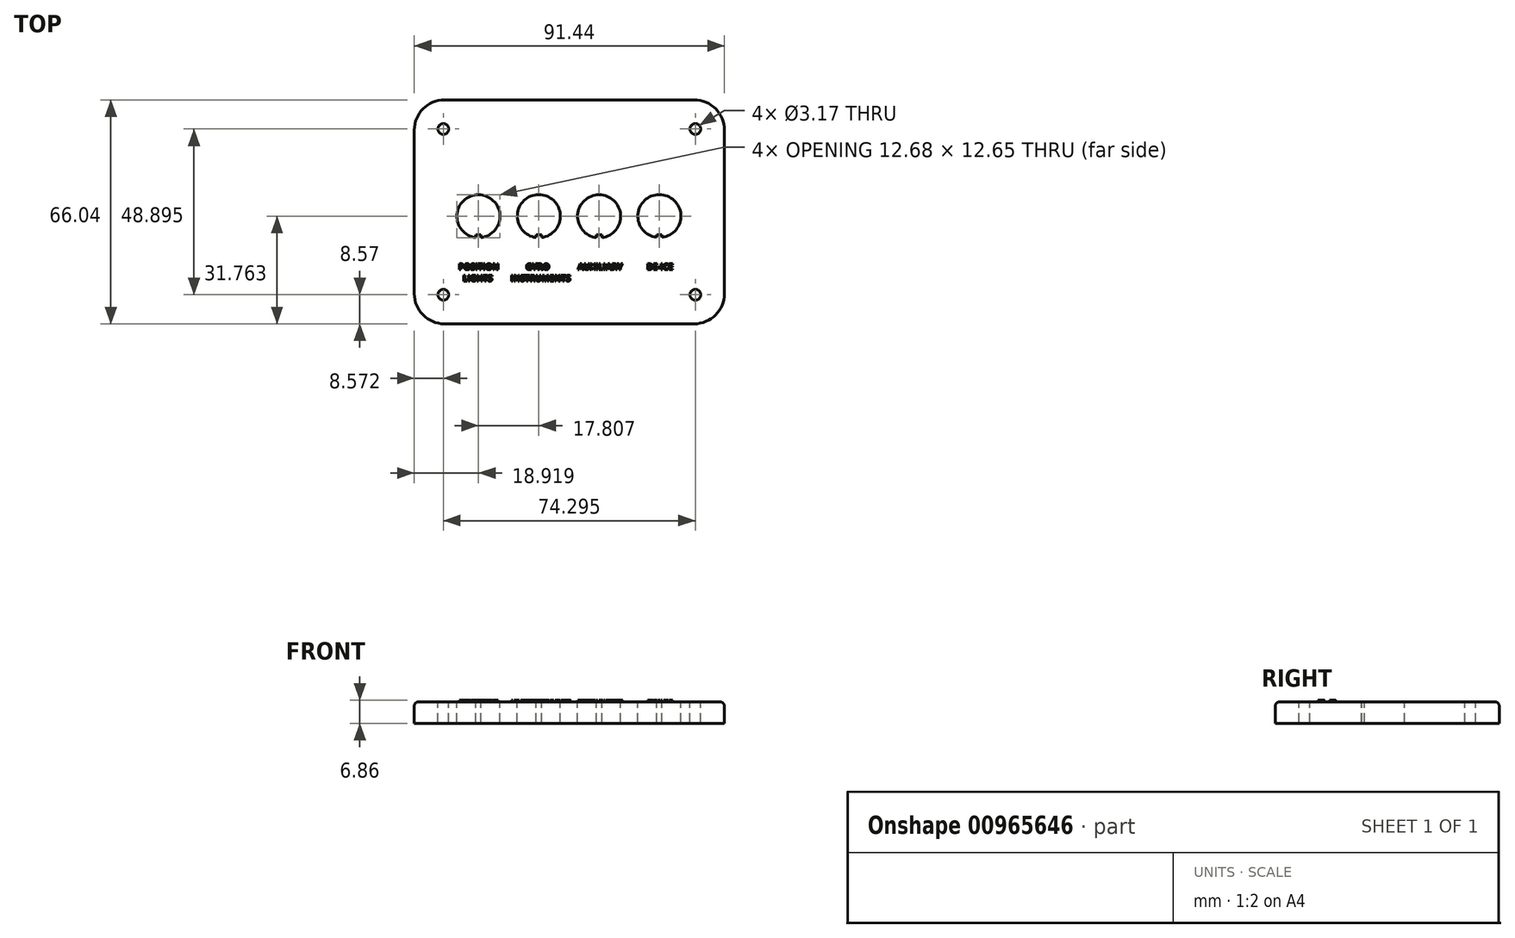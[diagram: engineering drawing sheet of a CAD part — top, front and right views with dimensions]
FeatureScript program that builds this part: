
annotation { "Feature Type Name" : "Feature", "Feature Type Description" : "" }
export const myFeature = defineFeature(function(context is Context, id is Id, definition is map)
    precondition{}
    {
        {
            var Q0;
            Q0=qCreatedBy(makeId("Top.planeOp"),FACE);
            var sketch = newSketch(context, id + "F0", { "sketchPlane" : qUnion([Q0])});
            skPoint(sketch, "E0.middle", {"position": v(-0.12, 0.03) * mm});
            skPoint(sketch, "E1.visualSharp", {"position": v(-44.57, 25.43) * mm});
            skArc(sketch, "E1.filletArc", {"start": v(-37.15, 28.28) * mm, "mid": v(-38.94, 27.54) * mm, "end": v(-39.69, 25.74) * mm});
            skPoint(sketch, "E2.visualSharp", {"position": v(44.33, 25.43) * mm});
            skArc(sketch, "E2.filletArc", {"start": v(39.69, 25.74) * mm, "mid": v(38.94, 27.54) * mm, "end": v(37.15, 28.28) * mm});
            skPoint(sketch, "E3.visualSharp", {"position": v(44.33, -25.37) * mm});
            skArc(sketch, "E3.filletArc", {"start": v(37.15, -25.7) * mm, "mid": v(38.94, -24.95) * mm, "end": v(39.69, -23.15) * mm});
            skPoint(sketch, "E4.visualSharp", {"position": v(-44.57, -25.37) * mm});
            skArc(sketch, "E4.filletArc", {"start": v(-39.69, -23.15) * mm, "mid": v(-38.94, -24.95) * mm, "end": v(-37.15, -25.7) * mm});
            skCircle(sketch, "E5", {"center": v(-37.15, 25.74) * mm, "radius": 1.59 * mm});
            skCircle(sketch, "E6", {"center": v(-37.15, -23.15) * mm, "radius": 1.59 * mm});
            skCircle(sketch, "E7", {"center": v(37.15, -23.15) * mm, "radius": 1.59 * mm});
            skCircle(sketch, "E8", {"center": v(37.15, 25.74) * mm, "radius": 1.59 * mm});
            skLineSegment(sketch, "E9.1", {"start": v(-33.65, -28.55) * mm, "end": v(33.66, -28.55) * mm});
            skLineSegment(sketch, "E9.2", {"start": v(-42.55, -19.66) * mm, "end": v(-42.55, 22.25) * mm});
            skLineSegment(sketch, "E9.5", {"start": v(-33.66, 31.14) * mm, "end": v(33.66, 31.14) * mm});
            skLineSegment(sketch, "E9.7", {"start": v(42.55, -19.66) * mm, "end": v(42.55, 22.25) * mm});
            skLineSegment(sketch, "E10.1", {"start": v(-36.83, -31.72) * mm, "end": v(36.83, -31.72) * mm});
            skLineSegment(sketch, "E10.2", {"start": v(-45.72, -22.83) * mm, "end": v(-45.72, 25.43) * mm});
            skLineSegment(sketch, "E10.5", {"start": v(-36.83, 34.32) * mm, "end": v(36.83, 34.32) * mm});
            skLineSegment(sketch, "E10.7", {"start": v(45.72, -22.83) * mm, "end": v(45.72, 25.43) * mm});
            skPoint(sketch, "E11", {"position": v(-26.79, 0) * mm});
            skPoint(sketch, "E12", {"position": v(-9, 0) * mm});
            skPoint(sketch, "E13", {"position": v(8.77, 0) * mm});
            skPoint(sketch, "E14", {"position": v(26.55, 0) * mm});
            skLineSegment(sketch, "E15.top", {"start": v(27.33, -5.38) * mm, "end": v(25.74, -5.38) * mm});
            skLineSegment(sketch, "E16", {"start": v(25.74, -6.25) * mm, "end": v(25.74, -5.38) * mm});
            skLineSegment(sketch, "E17", {"start": v(27.33, -6.25) * mm, "end": v(27.33, -5.38) * mm});
            skArc(sketch, "E18", {"start": v(27.33, -6.25) * mm, "mid": v(26.54, 6.4) * mm, "end": v(25.74, -6.25) * mm});
            skLineSegment(sketch, "E19.top", {"start": v(9.58, -5.43) * mm, "end": v(7.99, -5.43) * mm});
            skLineSegment(sketch, "E20", {"start": v(7.99, -6.3) * mm, "end": v(7.99, -5.43) * mm});
            skLineSegment(sketch, "E21", {"start": v(9.58, -6.3) * mm, "end": v(9.58, -5.43) * mm});
            skArc(sketch, "E22", {"start": v(9.58, -6.3) * mm, "mid": v(8.78, 6.35) * mm, "end": v(7.99, -6.3) * mm});
            skLineSegment(sketch, "E23.top", {"start": v(-8.2, -5.4) * mm, "end": v(-9.79, -5.4) * mm});
            skLineSegment(sketch, "E24", {"start": v(-9.79, -6.26) * mm, "end": v(-9.79, -5.4) * mm});
            skLineSegment(sketch, "E25", {"start": v(-8.2, -6.26) * mm, "end": v(-8.2, -5.4) * mm});
            skArc(sketch, "E26", {"start": v(-8.2, -6.26) * mm, "mid": v(-9, 6.4) * mm, "end": v(-9.79, -6.26) * mm});
            skLineSegment(sketch, "E27.top", {"start": v(-26, -5.42) * mm, "end": v(-27.6, -5.42) * mm});
            skLineSegment(sketch, "E28", {"start": v(-27.6, -6.28) * mm, "end": v(-27.6, -5.42) * mm});
            skLineSegment(sketch, "E29", {"start": v(-26, -6.28) * mm, "end": v(-26, -5.42) * mm});
            skArc(sketch, "E30", {"start": v(-26, -6.28) * mm, "mid": v(-26.8, 6.37) * mm, "end": v(-27.6, -6.28) * mm});
            skText(sketch, "E31", { "text": "POSITION\n  LIGHTS", "fontName": "OpenSans-Bold.ttf"});
            skText(sketch, "E32", { "text": "       GYRO\nINSTRUMENTS", "fontName": "OpenSans-Bold.ttf"});
            skText(sketch, "E33", { "text": "DE-ICE", "fontName": "OpenSans-Bold.ttf"});
            skText(sketch, "E34", { "text": "AUXILIARY", "fontName": "OpenSans-Bold.ttf"});
            skPoint(sketch, "E35.visualSharp", {"position": v(-45.72, 34.32) * mm});
            skArc(sketch, "E35.filletArc", {"start": v(-36.83, 34.32) * mm, "mid": v(-43.12, 31.71) * mm, "end": v(-45.72, 25.43) * mm});
            skPoint(sketch, "E36.visualSharp", {"position": v(45.72, 34.32) * mm});
            skArc(sketch, "E36.filletArc", {"start": v(45.72, 25.43) * mm, "mid": v(43.12, 31.71) * mm, "end": v(36.83, 34.32) * mm});
            skPoint(sketch, "E37.visualSharp", {"position": v(45.72, -31.72) * mm});
            skArc(sketch, "E37.filletArc", {"start": v(36.83, -31.72) * mm, "mid": v(43.12, -29.12) * mm, "end": v(45.72, -22.83) * mm});
            skPoint(sketch, "E38.visualSharp", {"position": v(-45.72, -31.72) * mm});
            skArc(sketch, "E38.filletArc", {"start": v(-45.72, -22.83) * mm, "mid": v(-43.12, -29.12) * mm, "end": v(-36.83, -31.72) * mm});
            skPoint(sketch, "E39.visualSharp", {"position": v(-42.55, -28.55) * mm});
            skArc(sketch, "E39.filletArc", {"start": v(-42.55, -19.66) * mm, "mid": v(-39.94, -25.94) * mm, "end": v(-33.65, -28.55) * mm});
            skPoint(sketch, "E40.visualSharp", {"position": v(-42.55, 31.14) * mm});
            skArc(sketch, "E40.filletArc", {"start": v(-33.66, 31.14) * mm, "mid": v(-39.94, 28.54) * mm, "end": v(-42.55, 22.25) * mm});
            skPoint(sketch, "E41.visualSharp", {"position": v(42.55, 31.14) * mm});
            skArc(sketch, "E41.filletArc", {"start": v(42.55, 22.25) * mm, "mid": v(39.94, 28.54) * mm, "end": v(33.66, 31.14) * mm});
            skPoint(sketch, "E42.visualSharp", {"position": v(42.55, -28.55) * mm});
            skArc(sketch, "E42.filletArc", {"start": v(33.66, -28.55) * mm, "mid": v(39.94, -25.94) * mm, "end": v(42.55, -19.66) * mm});
            const initialGuessF0  = {"E31": [-0.03267, -0.01575, 1, 0, 0.00178], "E32": [-0.0173, -0.01575, 1, 0, 0.00178], "E33": [0.02284, -0.01575, 1, 0, 0.00178], "E34": [0.00253, -0.01575, 1, 0, 0.00178]};
            skSetInitialGuess(sketch, initialGuessF0);
            skSolve(sketch);
        }
        {
            var Q0;
            Q0=makeQuery(id+"F0.imprint","IMPRINT",FACE,{"disambiguationData":[TD([[makeQuery(id+"F0.imprint","IMPRINT",EDGE,{"derivedFrom":sQuery(id+"F0.wireOp",EDGE,"E31.sketch_text.stroke-0")}),1.0]])]});
            var Q1;
            Q1=makeQuery(id+"F0.imprint","IMPRINT",FACE,{"disambiguationData":[TD([[makeQuery(id+"F0.imprint","IMPRINT",EDGE,{"derivedFrom":sQuery(id+"F0.wireOp",EDGE,"E31.sketch_text.stroke-24")}),1.0]])]});
            var Q2;
            Q2=makeQuery(id+"F0.imprint","IMPRINT",FACE,{"disambiguationData":[TD([[makeQuery(id+"F0.imprint","IMPRINT",EDGE,{"derivedFrom":sQuery(id+"F0.wireOp",EDGE,"E31.sketch_text.stroke-82")}),1.0]])]});
            var Q3;
            Q3=makeQuery(id+"F0.imprint","IMPRINT",FACE,{"disambiguationData":[TD([[makeQuery(id+"F0.imprint","IMPRINT",EDGE,{"derivedFrom":sQuery(id+"F0.wireOp",EDGE,"E33.sketch_text.stroke-7")}),1.0]])]});
            var Q4;
            Q4=makeQuery(id+"F0.imprint","IMPRINT",FACE,{"disambiguationData":[TD([[makeQuery(id+"F0.imprint","IMPRINT",EDGE,{"derivedFrom":sQuery(id+"F0.wireOp",EDGE,"E34.sketch_text.stroke-61")}),1.0]])]});
            var Q5;
            Q5=makeQuery(id+"F0.imprint","IMPRINT",FACE,{"disambiguationData":[TD([[makeQuery(id+"F0.imprint","IMPRINT",EDGE,{"derivedFrom":sQuery(id+"F0.wireOp",EDGE,"E34.sketch_text.stroke-65")}),1.0]])]});
            var Q6;
            Q6=makeQuery(id+"F0.imprint","IMPRINT",FACE,{"disambiguationData":[TD([[makeQuery(id+"F0.imprint","IMPRINT",EDGE,{"derivedFrom":sQuery(id+"F0.wireOp",EDGE,"E32.sketch_text.stroke-28")}),1.0]])]});
            var Q7;
            Q7=makeQuery(id+"F0.imprint","IMPRINT",FACE,{"disambiguationData":[TD([[makeQuery(id+"F0.imprint","IMPRINT",EDGE,{"derivedFrom":sQuery(id+"F0.wireOp",EDGE,"E32.sketch_text.stroke-115")}),1.0]])]});
            var Q8;
            Q8=makeQuery(id+"F0.imprint","IMPRINT",FACE,{"disambiguationData":[TD([[makeQuery(id+"F0.imprint","IMPRINT",EDGE,{"derivedFrom":sQuery(id+"F0.wireOp",EDGE,"E32.sketch_text.stroke-55")}),1.0]])]});
            var Q9;
            Q9=makeQuery(id+"F0.imprint","IMPRINT",FACE,{"disambiguationData":[TD([[makeQuery(id+"F0.imprint","IMPRINT",EDGE,{"derivedFrom":sQuery(id+"F0.wireOp",EDGE,"E34.sketch_text.stroke-8")}),1.0]])]});
            var Q10;
            Q10=makeQuery(id+"F0.imprint","IMPRINT",FACE,{"disambiguationData":[TD([[makeQuery(id+"F0.imprint","IMPRINT",EDGE,{"derivedFrom":sQuery(id+"F0.wireOp",EDGE,"E31.sketch_text.stroke-74")}),-1.0]])]});
            var Q11;
            Q11=makeQuery(id+"F0.imprint","IMPRINT",FACE,{"disambiguationData":[TD([[makeQuery(id+"F0.imprint","IMPRINT",EDGE,{"derivedFrom":sQuery(id+"F0.wireOp",EDGE,"E31.sketch_text.stroke-88")}),-1.0]])]});
            var Q12;
            Q12=makeQuery(id+"F0.imprint","IMPRINT",FACE,{"disambiguationData":[TD([[makeQuery(id+"F0.imprint","IMPRINT",EDGE,{"derivedFrom":sQuery(id+"F0.wireOp",EDGE,"E32.sketch_text.stroke-47")}),-1.0]])]});
            var Q13;
            Q13=makeQuery(id+"F0.imprint","IMPRINT",FACE,{"disambiguationData":[TD([[makeQuery(id+"F0.imprint","IMPRINT",EDGE,{"derivedFrom":sQuery(id+"F0.wireOp",EDGE,"E32.sketch_text.stroke-28")}),-1.0]])]});
            var Q14;
            Q14=makeQuery(id+"F0.imprint","IMPRINT",FACE,{"disambiguationData":[TD([[makeQuery(id+"F0.imprint","IMPRINT",EDGE,{"derivedFrom":sQuery(id+"F0.wireOp",EDGE,"E32.sketch_text.stroke-19")}),-1.0]])]});
            var Q15;
            Q15=makeQuery(id+"F0.imprint","IMPRINT",FACE,{"disambiguationData":[TD([[makeQuery(id+"F0.imprint","IMPRINT",EDGE,{"derivedFrom":sQuery(id+"F0.wireOp",EDGE,"E32.sketch_text.stroke-0")}),-1.0]])]});
            var Q16;
            Q16=makeQuery(id+"F0.imprint","IMPRINT",FACE,{"disambiguationData":[TD([[makeQuery(id+"F0.imprint","IMPRINT",EDGE,{"derivedFrom":sQuery(id+"F0.wireOp",EDGE,"E32.sketch_text.stroke-168")}),-1.0]])]});
            var Q17;
            Q17=makeQuery(id+"F0.imprint","IMPRINT",FACE,{"disambiguationData":[TD([[makeQuery(id+"F0.imprint","IMPRINT",EDGE,{"derivedFrom":sQuery(id+"F0.wireOp",EDGE,"E32.sketch_text.stroke-180")}),-1.0]])]});
            var Q18;
            Q18=makeQuery(id+"F0.imprint","IMPRINT",FACE,{"disambiguationData":[TD([[makeQuery(id+"F0.imprint","IMPRINT",EDGE,{"derivedFrom":sQuery(id+"F0.wireOp",EDGE,"E32.sketch_text.stroke-194")}),-1.0]])]});
            var Q19;
            Q19=makeQuery(id+"F0.imprint","IMPRINT",FACE,{"disambiguationData":[TD([[makeQuery(id+"F0.imprint","IMPRINT",EDGE,{"derivedFrom":sQuery(id+"F0.wireOp",EDGE,"E32.sketch_text.stroke-202")}),-1.0]])]});
            var Q20;
            Q20=makeQuery(id+"F0.imprint","IMPRINT",FACE,{"disambiguationData":[TD([[makeQuery(id+"F0.imprint","IMPRINT",EDGE,{"derivedFrom":sQuery(id+"F0.wireOp",EDGE,"E31.sketch_text.stroke-102")}),-1.0]])]});
            var Q21;
            Q21=makeQuery(id+"F0.imprint","IMPRINT",FACE,{"disambiguationData":[TD([[makeQuery(id+"F0.imprint","IMPRINT",EDGE,{"derivedFrom":sQuery(id+"F0.wireOp",EDGE,"E31.sketch_text.stroke-108")}),-1.0]])]});
            var Q22;
            Q22=makeQuery(id+"F0.imprint","IMPRINT",FACE,{"disambiguationData":[TD([[makeQuery(id+"F0.imprint","IMPRINT",EDGE,{"derivedFrom":sQuery(id+"F0.wireOp",EDGE,"E31.sketch_text.stroke-112")}),-1.0]])]});
            var Q23;
            Q23=makeQuery(id+"F0.imprint","IMPRINT",FACE,{"disambiguationData":[TD([[makeQuery(id+"F0.imprint","IMPRINT",EDGE,{"derivedFrom":sQuery(id+"F0.wireOp",EDGE,"E31.sketch_text.stroke-131")}),-1.0]])]});
            var Q24;
            Q24=makeQuery(id+"F0.imprint","IMPRINT",FACE,{"disambiguationData":[TD([[makeQuery(id+"F0.imprint","IMPRINT",EDGE,{"derivedFrom":sQuery(id+"F0.wireOp",EDGE,"E31.sketch_text.stroke-143")}),-1.0]])]});
            var Q25;
            Q25=makeQuery(id+"F0.imprint","IMPRINT",FACE,{"disambiguationData":[TD([[makeQuery(id+"F0.imprint","IMPRINT",EDGE,{"derivedFrom":sQuery(id+"F0.wireOp",EDGE,"E31.sketch_text.stroke-151")}),-1.0]])]});
            var Q26;
            Q26=makeQuery(id+"F0.imprint","IMPRINT",FACE,{"disambiguationData":[TD([[makeQuery(id+"F0.imprint","IMPRINT",EDGE,{"derivedFrom":sQuery(id+"F0.wireOp",EDGE,"E31.sketch_text.stroke-70")}),-1.0]])]});
            var Q27;
            Q27=makeQuery(id+"F0.imprint","IMPRINT",FACE,{"disambiguationData":[TD([[makeQuery(id+"F0.imprint","IMPRINT",EDGE,{"derivedFrom":sQuery(id+"F0.wireOp",EDGE,"E31.sketch_text.stroke-62")}),-1.0]])]});
            var Q28;
            Q28=makeQuery(id+"F0.imprint","IMPRINT",FACE,{"disambiguationData":[TD([[makeQuery(id+"F0.imprint","IMPRINT",EDGE,{"derivedFrom":sQuery(id+"F0.wireOp",EDGE,"E31.sketch_text.stroke-58")}),-1.0]])]});
            var Q29;
            Q29=makeQuery(id+"F0.imprint","IMPRINT",FACE,{"disambiguationData":[TD([[makeQuery(id+"F0.imprint","IMPRINT",EDGE,{"derivedFrom":sQuery(id+"F0.wireOp",EDGE,"E31.sketch_text.stroke-30")}),-1.0]])]});
            var Q30;
            Q30=makeQuery(id+"F0.imprint","IMPRINT",FACE,{"disambiguationData":[TD([[makeQuery(id+"F0.imprint","IMPRINT",EDGE,{"derivedFrom":sQuery(id+"F0.wireOp",EDGE,"E31.sketch_text.stroke-16")}),-1.0]])]});
            var Q31;
            Q31=makeQuery(id+"F0.imprint","IMPRINT",FACE,{"disambiguationData":[TD([[makeQuery(id+"F0.imprint","IMPRINT",EDGE,{"derivedFrom":sQuery(id+"F0.wireOp",EDGE,"E31.sketch_text.stroke-0")}),-1.0]])]});
            var Q32;
            Q32=makeQuery(id+"F0.imprint","IMPRINT",FACE,{"disambiguationData":[TD([[makeQuery(id+"F0.imprint","IMPRINT",EDGE,{"derivedFrom":sQuery(id+"F0.wireOp",EDGE,"E32.sketch_text.stroke-61")}),-1.0]])]});
            var Q33;
            Q33=makeQuery(id+"F0.imprint","IMPRINT",FACE,{"disambiguationData":[TD([[makeQuery(id+"F0.imprint","IMPRINT",EDGE,{"derivedFrom":sQuery(id+"F0.wireOp",EDGE,"E32.sketch_text.stroke-65")}),-1.0]])]});
            var Q34;
            Q34=makeQuery(id+"F0.imprint","IMPRINT",FACE,{"disambiguationData":[TD([[makeQuery(id+"F0.imprint","IMPRINT",EDGE,{"derivedFrom":sQuery(id+"F0.wireOp",EDGE,"E32.sketch_text.stroke-79")}),-1.0]])]});
            var Q35;
            Q35=makeQuery(id+"F0.imprint","IMPRINT",FACE,{"disambiguationData":[TD([[makeQuery(id+"F0.imprint","IMPRINT",EDGE,{"derivedFrom":sQuery(id+"F0.wireOp",EDGE,"E32.sketch_text.stroke-107")}),-1.0]])]});
            var Q36;
            Q36=makeQuery(id+"F0.imprint","IMPRINT",FACE,{"disambiguationData":[TD([[makeQuery(id+"F0.imprint","IMPRINT",EDGE,{"derivedFrom":sQuery(id+"F0.wireOp",EDGE,"E32.sketch_text.stroke-115")}),-1.0]])]});
            var Q37;
            Q37=makeQuery(id+"F0.imprint","IMPRINT",FACE,{"disambiguationData":[TD([[makeQuery(id+"F0.imprint","IMPRINT",EDGE,{"derivedFrom":sQuery(id+"F0.wireOp",EDGE,"E32.sketch_text.stroke-134")}),-1.0]])]});
            var Q38;
            Q38=makeQuery(id+"F0.imprint","IMPRINT",FACE,{"disambiguationData":[TD([[makeQuery(id+"F0.imprint","IMPRINT",EDGE,{"derivedFrom":sQuery(id+"F0.wireOp",EDGE,"E32.sketch_text.stroke-149")}),-1.0]])]});
            var Q39;
            Q39=makeQuery(id+"F0.imprint","IMPRINT",FACE,{"disambiguationData":[TD([[makeQuery(id+"F0.imprint","IMPRINT",EDGE,{"derivedFrom":sQuery(id+"F0.wireOp",EDGE,"E34.sketch_text.stroke-84")}),-1.0]])]});
            var Q40;
            Q40=makeQuery(id+"F0.imprint","IMPRINT",FACE,{"disambiguationData":[TD([[makeQuery(id+"F0.imprint","IMPRINT",EDGE,{"derivedFrom":sQuery(id+"F0.wireOp",EDGE,"E34.sketch_text.stroke-65")}),-1.0]])]});
            var Q41;
            Q41=makeQuery(id+"F0.imprint","IMPRINT",FACE,{"disambiguationData":[TD([[makeQuery(id+"F0.imprint","IMPRINT",EDGE,{"derivedFrom":sQuery(id+"F0.wireOp",EDGE,"E34.sketch_text.stroke-53")}),-1.0]])]});
            var Q42;
            Q42=makeQuery(id+"F0.imprint","IMPRINT",FACE,{"disambiguationData":[TD([[makeQuery(id+"F0.imprint","IMPRINT",EDGE,{"derivedFrom":sQuery(id+"F0.wireOp",EDGE,"E34.sketch_text.stroke-49")}),-1.0]])]});
            var Q43;
            Q43=makeQuery(id+"F0.imprint","IMPRINT",FACE,{"disambiguationData":[TD([[makeQuery(id+"F0.imprint","IMPRINT",EDGE,{"derivedFrom":sQuery(id+"F0.wireOp",EDGE,"E34.sketch_text.stroke-43")}),-1.0]])]});
            var Q44;
            Q44=makeQuery(id+"F0.imprint","IMPRINT",FACE,{"disambiguationData":[TD([[makeQuery(id+"F0.imprint","IMPRINT",EDGE,{"derivedFrom":sQuery(id+"F0.wireOp",EDGE,"E34.sketch_text.stroke-39")}),-1.0]])]});
            var Q45;
            Q45=makeQuery(id+"F0.imprint","IMPRINT",FACE,{"disambiguationData":[TD([[makeQuery(id+"F0.imprint","IMPRINT",EDGE,{"derivedFrom":sQuery(id+"F0.wireOp",EDGE,"E34.sketch_text.stroke-27")}),-1.0]])]});
            var Q46;
            Q46=makeQuery(id+"F0.imprint","IMPRINT",FACE,{"disambiguationData":[TD([[makeQuery(id+"F0.imprint","IMPRINT",EDGE,{"derivedFrom":sQuery(id+"F0.wireOp",EDGE,"E34.sketch_text.stroke-12")}),-1.0]])]});
            var Q47;
            Q47=makeQuery(id+"F0.imprint","IMPRINT",FACE,{"disambiguationData":[TD([[makeQuery(id+"F0.imprint","IMPRINT",EDGE,{"derivedFrom":sQuery(id+"F0.wireOp",EDGE,"E34.sketch_text.stroke-0")}),-1.0]])]});
            var Q48;
            Q48=makeQuery(id+"F0.imprint","IMPRINT",FACE,{"disambiguationData":[TD([[makeQuery(id+"F0.imprint","IMPRINT",EDGE,{"derivedFrom":sQuery(id+"F0.wireOp",EDGE,"E33.sketch_text.stroke-0")}),-1.0]])]});
            var Q49;
            Q49=makeQuery(id+"F0.imprint","IMPRINT",FACE,{"disambiguationData":[TD([[makeQuery(id+"F0.imprint","IMPRINT",EDGE,{"derivedFrom":sQuery(id+"F0.wireOp",EDGE,"E33.sketch_text.stroke-12")}),-1.0]])]});
            var Q50;
            Q50=makeQuery(id+"F0.imprint","IMPRINT",FACE,{"disambiguationData":[TD([[makeQuery(id+"F0.imprint","IMPRINT",EDGE,{"derivedFrom":sQuery(id+"F0.wireOp",EDGE,"E33.sketch_text.stroke-24")}),-1.0]])]});
            var Q51;
            Q51=makeQuery(id+"F0.imprint","IMPRINT",FACE,{"disambiguationData":[TD([[makeQuery(id+"F0.imprint","IMPRINT",EDGE,{"derivedFrom":sQuery(id+"F0.wireOp",EDGE,"E33.sketch_text.stroke-28")}),-1.0]])]});
            var Q52;
            Q52=makeQuery(id+"F0.imprint","IMPRINT",FACE,{"disambiguationData":[TD([[makeQuery(id+"F0.imprint","IMPRINT",EDGE,{"derivedFrom":sQuery(id+"F0.wireOp",EDGE,"E33.sketch_text.stroke-32")}),-1.0]])]});
            var Q53;
            Q53=makeQuery(id+"F0.imprint","IMPRINT",FACE,{"disambiguationData":[TD([[makeQuery(id+"F0.imprint","IMPRINT",EDGE,{"derivedFrom":sQuery(id+"F0.wireOp",EDGE,"E33.sketch_text.stroke-47")}),-1.0]])]});
            var Q54;
            Q54=makeQuery(id+"F0.imprint","IMPRINT",FACE,{"disambiguationData":[TD([[makeQuery(id+"F0.imprint","IMPRINT",EDGE,{"derivedFrom":sQuery(id+"F0.wireOp",EDGE,"E9.1")}),-1.0]])]});
            var Q55;
            Q55=makeQuery(id+"F0.imprint","IMPRINT",FACE,{"disambiguationData":[TD([[makeQuery(id+"F0.imprint","IMPRINT",EDGE,{"derivedFrom":sQuery(id+"F0.wireOp",EDGE,"E5")}),-1.0]])]});
            extrude(context, id + "F1", {"entities" : qUnion([Q0, Q1, Q2, Q3, Q4, Q5, Q6, Q7, Q8, Q9, Q10, Q11, Q12, Q13, Q14, Q15, Q16, Q17, Q18, Q19, Q20, Q21, Q22, Q23, Q24, Q25, Q26, Q27, Q28, Q29, Q30, Q31, Q32, Q33, Q34, Q35, Q36, Q37, Q38, Q39, Q40, Q41, Q42, Q43, Q44, Q45, Q46, Q47, Q48, Q49, Q50, Q51, Q52, Q53, Q54, Q55]), "oppositeDirection" : true, "depth" : 6.35 * mm, "offsetDistance" : 25.4 * mm});
        }
        {
            var Q0;
            Q0=makeQuery(id+"F1.opExtrude","CAP_EDGE",EDGE,{"disambiguationData":[OSD([sQuery(id+"F0.wireOp",EDGE,"E10.7")])],"isStart":true});
            fillet(context, id + "F2", {"entities" : qUnion([Q0]), "radius" : 1.27 * mm, "tangentPropagation" : true, "allowEdgeOverflow" : false});
        }
        {
            var Q0;
            Q0=makeQuery(id+"F0.imprint","IMPRINT",FACE,{"disambiguationData":[TD([[makeQuery(id+"F0.imprint","IMPRINT",EDGE,{"derivedFrom":sQuery(id+"F0.wireOp",EDGE,"E31.sketch_text.stroke-16")}),-1.0]])]});
            var Q1;
            Q1=makeQuery(id+"F0.imprint","IMPRINT",FACE,{"disambiguationData":[TD([[makeQuery(id+"F0.imprint","IMPRINT",EDGE,{"derivedFrom":sQuery(id+"F0.wireOp",EDGE,"E31.sketch_text.stroke-0")}),-1.0]])]});
            var Q2;
            Q2=makeQuery(id+"F0.imprint","IMPRINT",FACE,{"disambiguationData":[TD([[makeQuery(id+"F0.imprint","IMPRINT",EDGE,{"derivedFrom":sQuery(id+"F0.wireOp",EDGE,"E31.sketch_text.stroke-30")}),-1.0]])]});
            var Q3;
            Q3=makeQuery(id+"F0.imprint","IMPRINT",FACE,{"disambiguationData":[TD([[makeQuery(id+"F0.imprint","IMPRINT",EDGE,{"derivedFrom":sQuery(id+"F0.wireOp",EDGE,"E31.sketch_text.stroke-58")}),-1.0]])]});
            var Q4;
            Q4=makeQuery(id+"F0.imprint","IMPRINT",FACE,{"disambiguationData":[TD([[makeQuery(id+"F0.imprint","IMPRINT",EDGE,{"derivedFrom":sQuery(id+"F0.wireOp",EDGE,"E31.sketch_text.stroke-62")}),-1.0]])]});
            var Q5;
            Q5=makeQuery(id+"F0.imprint","IMPRINT",FACE,{"disambiguationData":[TD([[makeQuery(id+"F0.imprint","IMPRINT",EDGE,{"derivedFrom":sQuery(id+"F0.wireOp",EDGE,"E31.sketch_text.stroke-70")}),-1.0]])]});
            var Q6;
            Q6=makeQuery(id+"F0.imprint","IMPRINT",FACE,{"disambiguationData":[TD([[makeQuery(id+"F0.imprint","IMPRINT",EDGE,{"derivedFrom":sQuery(id+"F0.wireOp",EDGE,"E31.sketch_text.stroke-131")}),-1.0]])]});
            var Q7;
            Q7=makeQuery(id+"F0.imprint","IMPRINT",FACE,{"disambiguationData":[TD([[makeQuery(id+"F0.imprint","IMPRINT",EDGE,{"derivedFrom":sQuery(id+"F0.wireOp",EDGE,"E31.sketch_text.stroke-112")}),-1.0]])]});
            var Q8;
            Q8=makeQuery(id+"F0.imprint","IMPRINT",FACE,{"disambiguationData":[TD([[makeQuery(id+"F0.imprint","IMPRINT",EDGE,{"derivedFrom":sQuery(id+"F0.wireOp",EDGE,"E31.sketch_text.stroke-108")}),-1.0]])]});
            var Q9;
            Q9=makeQuery(id+"F0.imprint","IMPRINT",FACE,{"disambiguationData":[TD([[makeQuery(id+"F0.imprint","IMPRINT",EDGE,{"derivedFrom":sQuery(id+"F0.wireOp",EDGE,"E31.sketch_text.stroke-102")}),-1.0]])]});
            var Q10;
            Q10=makeQuery(id+"F0.imprint","IMPRINT",FACE,{"disambiguationData":[TD([[makeQuery(id+"F0.imprint","IMPRINT",EDGE,{"derivedFrom":sQuery(id+"F0.wireOp",EDGE,"E31.sketch_text.stroke-74")}),-1.0]])]});
            var Q11;
            Q11=makeQuery(id+"F0.imprint","IMPRINT",FACE,{"disambiguationData":[TD([[makeQuery(id+"F0.imprint","IMPRINT",EDGE,{"derivedFrom":sQuery(id+"F0.wireOp",EDGE,"E31.sketch_text.stroke-88")}),-1.0]])]});
            var Q12;
            Q12=makeQuery(id+"F0.imprint","IMPRINT",FACE,{"disambiguationData":[TD([[makeQuery(id+"F0.imprint","IMPRINT",EDGE,{"derivedFrom":sQuery(id+"F0.wireOp",EDGE,"E31.sketch_text.stroke-143")}),-1.0]])]});
            var Q13;
            Q13=makeQuery(id+"F0.imprint","IMPRINT",FACE,{"disambiguationData":[TD([[makeQuery(id+"F0.imprint","IMPRINT",EDGE,{"derivedFrom":sQuery(id+"F0.wireOp",EDGE,"E31.sketch_text.stroke-151")}),-1.0]])]});
            var Q14;
            Q14=makeQuery(id+"F0.imprint","IMPRINT",FACE,{"disambiguationData":[TD([[makeQuery(id+"F0.imprint","IMPRINT",EDGE,{"derivedFrom":sQuery(id+"F0.wireOp",EDGE,"E32.sketch_text.stroke-28")}),-1.0]])]});
            var Q15;
            Q15=makeQuery(id+"F0.imprint","IMPRINT",FACE,{"disambiguationData":[TD([[makeQuery(id+"F0.imprint","IMPRINT",EDGE,{"derivedFrom":sQuery(id+"F0.wireOp",EDGE,"E32.sketch_text.stroke-19")}),-1.0]])]});
            var Q16;
            Q16=makeQuery(id+"F0.imprint","IMPRINT",FACE,{"disambiguationData":[TD([[makeQuery(id+"F0.imprint","IMPRINT",EDGE,{"derivedFrom":sQuery(id+"F0.wireOp",EDGE,"E32.sketch_text.stroke-0")}),-1.0]])]});
            var Q17;
            Q17=makeQuery(id+"F0.imprint","IMPRINT",FACE,{"disambiguationData":[TD([[makeQuery(id+"F0.imprint","IMPRINT",EDGE,{"derivedFrom":sQuery(id+"F0.wireOp",EDGE,"E32.sketch_text.stroke-134")}),-1.0]])]});
            var Q18;
            Q18=makeQuery(id+"F0.imprint","IMPRINT",FACE,{"disambiguationData":[TD([[makeQuery(id+"F0.imprint","IMPRINT",EDGE,{"derivedFrom":sQuery(id+"F0.wireOp",EDGE,"E32.sketch_text.stroke-115")}),-1.0]])]});
            var Q19;
            Q19=makeQuery(id+"F0.imprint","IMPRINT",FACE,{"disambiguationData":[TD([[makeQuery(id+"F0.imprint","IMPRINT",EDGE,{"derivedFrom":sQuery(id+"F0.wireOp",EDGE,"E32.sketch_text.stroke-79")}),-1.0]])]});
            var Q20;
            Q20=makeQuery(id+"F0.imprint","IMPRINT",FACE,{"disambiguationData":[TD([[makeQuery(id+"F0.imprint","IMPRINT",EDGE,{"derivedFrom":sQuery(id+"F0.wireOp",EDGE,"E32.sketch_text.stroke-65")}),-1.0]])]});
            var Q21;
            Q21=makeQuery(id+"F0.imprint","IMPRINT",FACE,{"disambiguationData":[TD([[makeQuery(id+"F0.imprint","IMPRINT",EDGE,{"derivedFrom":sQuery(id+"F0.wireOp",EDGE,"E32.sketch_text.stroke-61")}),-1.0]])]});
            var Q22;
            Q22=makeQuery(id+"F0.imprint","IMPRINT",FACE,{"disambiguationData":[TD([[makeQuery(id+"F0.imprint","IMPRINT",EDGE,{"derivedFrom":sQuery(id+"F0.wireOp",EDGE,"E32.sketch_text.stroke-107")}),-1.0]])]});
            var Q23;
            Q23=makeQuery(id+"F0.imprint","IMPRINT",FACE,{"disambiguationData":[TD([[makeQuery(id+"F0.imprint","IMPRINT",EDGE,{"derivedFrom":sQuery(id+"F0.wireOp",EDGE,"E32.sketch_text.stroke-47")}),-1.0]])]});
            var Q24;
            Q24=makeQuery(id+"F0.imprint","IMPRINT",FACE,{"disambiguationData":[TD([[makeQuery(id+"F0.imprint","IMPRINT",EDGE,{"derivedFrom":sQuery(id+"F0.wireOp",EDGE,"E32.sketch_text.stroke-149")}),-1.0]])]});
            var Q25;
            Q25=makeQuery(id+"F0.imprint","IMPRINT",FACE,{"disambiguationData":[TD([[makeQuery(id+"F0.imprint","IMPRINT",EDGE,{"derivedFrom":sQuery(id+"F0.wireOp",EDGE,"E32.sketch_text.stroke-168")}),-1.0]])]});
            var Q26;
            Q26=makeQuery(id+"F0.imprint","IMPRINT",FACE,{"disambiguationData":[TD([[makeQuery(id+"F0.imprint","IMPRINT",EDGE,{"derivedFrom":sQuery(id+"F0.wireOp",EDGE,"E32.sketch_text.stroke-180")}),-1.0]])]});
            var Q27;
            Q27=makeQuery(id+"F0.imprint","IMPRINT",FACE,{"disambiguationData":[TD([[makeQuery(id+"F0.imprint","IMPRINT",EDGE,{"derivedFrom":sQuery(id+"F0.wireOp",EDGE,"E32.sketch_text.stroke-194")}),-1.0]])]});
            var Q28;
            Q28=makeQuery(id+"F0.imprint","IMPRINT",FACE,{"disambiguationData":[TD([[makeQuery(id+"F0.imprint","IMPRINT",EDGE,{"derivedFrom":sQuery(id+"F0.wireOp",EDGE,"E32.sketch_text.stroke-202")}),-1.0]])]});
            var Q29;
            Q29=makeQuery(id+"F0.imprint","IMPRINT",FACE,{"disambiguationData":[TD([[makeQuery(id+"F0.imprint","IMPRINT",EDGE,{"derivedFrom":sQuery(id+"F0.wireOp",EDGE,"E34.sketch_text.stroke-84")}),-1.0]])]});
            var Q30;
            Q30=makeQuery(id+"F0.imprint","IMPRINT",FACE,{"disambiguationData":[TD([[makeQuery(id+"F0.imprint","IMPRINT",EDGE,{"derivedFrom":sQuery(id+"F0.wireOp",EDGE,"E34.sketch_text.stroke-65")}),-1.0]])]});
            var Q31;
            Q31=makeQuery(id+"F0.imprint","IMPRINT",FACE,{"disambiguationData":[TD([[makeQuery(id+"F0.imprint","IMPRINT",EDGE,{"derivedFrom":sQuery(id+"F0.wireOp",EDGE,"E34.sketch_text.stroke-53")}),-1.0]])]});
            var Q32;
            Q32=makeQuery(id+"F0.imprint","IMPRINT",FACE,{"disambiguationData":[TD([[makeQuery(id+"F0.imprint","IMPRINT",EDGE,{"derivedFrom":sQuery(id+"F0.wireOp",EDGE,"E34.sketch_text.stroke-49")}),-1.0]])]});
            var Q33;
            Q33=makeQuery(id+"F0.imprint","IMPRINT",FACE,{"disambiguationData":[TD([[makeQuery(id+"F0.imprint","IMPRINT",EDGE,{"derivedFrom":sQuery(id+"F0.wireOp",EDGE,"E34.sketch_text.stroke-43")}),-1.0]])]});
            var Q34;
            Q34=makeQuery(id+"F0.imprint","IMPRINT",FACE,{"disambiguationData":[TD([[makeQuery(id+"F0.imprint","IMPRINT",EDGE,{"derivedFrom":sQuery(id+"F0.wireOp",EDGE,"E34.sketch_text.stroke-39")}),-1.0]])]});
            var Q35;
            Q35=makeQuery(id+"F0.imprint","IMPRINT",FACE,{"disambiguationData":[TD([[makeQuery(id+"F0.imprint","IMPRINT",EDGE,{"derivedFrom":sQuery(id+"F0.wireOp",EDGE,"E34.sketch_text.stroke-27")}),-1.0]])]});
            var Q36;
            Q36=makeQuery(id+"F0.imprint","IMPRINT",FACE,{"disambiguationData":[TD([[makeQuery(id+"F0.imprint","IMPRINT",EDGE,{"derivedFrom":sQuery(id+"F0.wireOp",EDGE,"E34.sketch_text.stroke-12")}),-1.0]])]});
            var Q37;
            Q37=makeQuery(id+"F0.imprint","IMPRINT",FACE,{"disambiguationData":[TD([[makeQuery(id+"F0.imprint","IMPRINT",EDGE,{"derivedFrom":sQuery(id+"F0.wireOp",EDGE,"E34.sketch_text.stroke-0")}),-1.0]])]});
            var Q38;
            Q38=makeQuery(id+"F0.imprint","IMPRINT",FACE,{"disambiguationData":[TD([[makeQuery(id+"F0.imprint","IMPRINT",EDGE,{"derivedFrom":sQuery(id+"F0.wireOp",EDGE,"E33.sketch_text.stroke-0")}),-1.0]])]});
            var Q39;
            Q39=makeQuery(id+"F0.imprint","IMPRINT",FACE,{"disambiguationData":[TD([[makeQuery(id+"F0.imprint","IMPRINT",EDGE,{"derivedFrom":sQuery(id+"F0.wireOp",EDGE,"E33.sketch_text.stroke-12")}),-1.0]])]});
            var Q40;
            Q40=makeQuery(id+"F0.imprint","IMPRINT",FACE,{"disambiguationData":[TD([[makeQuery(id+"F0.imprint","IMPRINT",EDGE,{"derivedFrom":sQuery(id+"F0.wireOp",EDGE,"E33.sketch_text.stroke-24")}),-1.0]])]});
            var Q41;
            Q41=makeQuery(id+"F0.imprint","IMPRINT",FACE,{"disambiguationData":[TD([[makeQuery(id+"F0.imprint","IMPRINT",EDGE,{"derivedFrom":sQuery(id+"F0.wireOp",EDGE,"E33.sketch_text.stroke-28")}),-1.0]])]});
            var Q42;
            Q42=makeQuery(id+"F0.imprint","IMPRINT",FACE,{"disambiguationData":[TD([[makeQuery(id+"F0.imprint","IMPRINT",EDGE,{"derivedFrom":sQuery(id+"F0.wireOp",EDGE,"E33.sketch_text.stroke-32")}),-1.0]])]});
            var Q43;
            Q43=makeQuery(id+"F0.imprint","IMPRINT",FACE,{"disambiguationData":[TD([[makeQuery(id+"F0.imprint","IMPRINT",EDGE,{"derivedFrom":sQuery(id+"F0.wireOp",EDGE,"E33.sketch_text.stroke-47")}),-1.0]])]});
            extrude(context, id + "F3", {"entities" : qUnion([Q0, Q1, Q2, Q3, Q4, Q5, Q6, Q7, Q8, Q9, Q10, Q11, Q12, Q13, Q14, Q15, Q16, Q17, Q18, Q19, Q20, Q21, Q22, Q23, Q24, Q25, Q26, Q27, Q28, Q29, Q30, Q31, Q32, Q33, Q34, Q35, Q36, Q37, Q38, Q39, Q40, Q41, Q42, Q43]), "operationType" : NewBodyOperationType.ADD, "depth" : 0.5 * mm, "offsetDistance" : 25.4 * mm});
        }
    });
